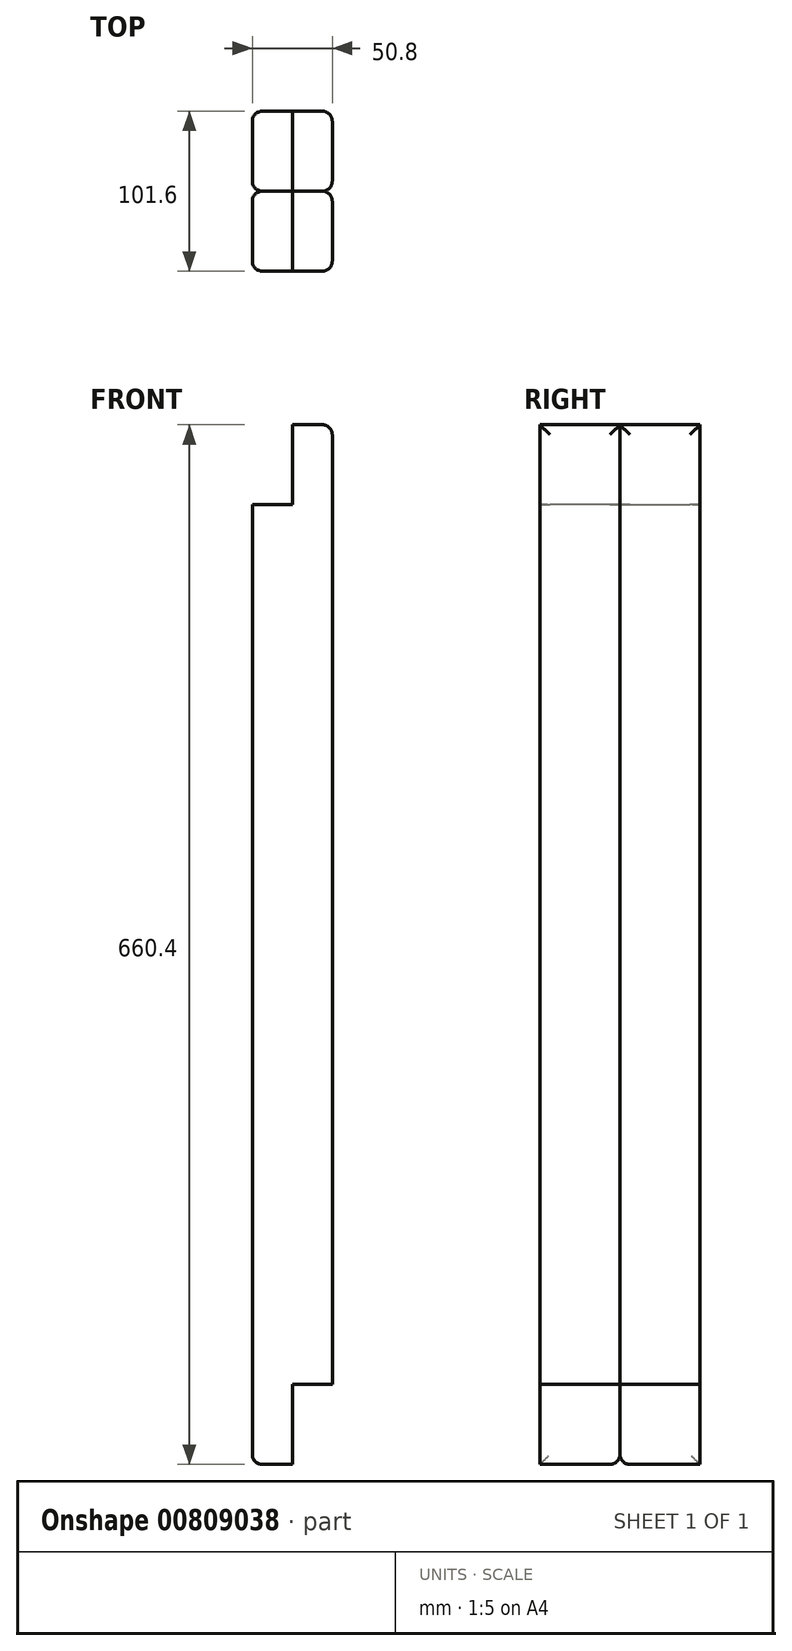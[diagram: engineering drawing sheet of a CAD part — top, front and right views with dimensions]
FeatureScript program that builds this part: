
annotation { "Feature Type Name" : "Feature", "Feature Type Description" : "" }
export const myFeature = defineFeature(function(context is Context, id is Id, definition is map)
    precondition{}
    {
        {
            var Q0;
            Q0=qCreatedBy(makeId("Top.planeOp"),FACE);
            var sketch = newSketch(context, id + "F0", { "sketchPlane" : qUnion([Q0])});
            skLineSegment(sketch, "E0.bottom", {"start": v(0, 0) * mm, "end": v(25.4, 0) * mm});
            skLineSegment(sketch, "E0.top", {"start": v(0, 50.8) * mm, "end": v(25.4, 50.8) * mm});
            skLineSegment(sketch, "E0.left", {"start": v(0, 0) * mm, "end": v(0, 50.8) * mm});
            skLineSegment(sketch, "E0.right", {"start": v(25.4, 0) * mm, "end": v(25.4, 50.8) * mm});
            skLineSegment(sketch, "E1.bottom", {"start": v(0, 0) * mm, "end": v(-25.4, 0) * mm});
            skLineSegment(sketch, "E1.top", {"start": v(0, 50.8) * mm, "end": v(-25.4, 50.8) * mm});
            skLineSegment(sketch, "E1.right", {"start": v(-25.4, 0) * mm, "end": v(-25.4, 50.8) * mm});
            skSolve(sketch);
        }
        {
            var Q0;
            Q0=makeQuery(id+"F0.imprint","IMPRINT",FACE,{"disambiguationData":[TD([[makeQuery(id+"F0.imprint","IMPRINT",EDGE,{"derivedFrom":sQuery(id+"F0.wireOp",EDGE,"E0.bottom")}),1.0]])]});
            extrude(context, id + "F1", {"entities" : qUnion([Q0]), "depth" : 609.6 * mm, "offsetDistance" : 25.4 * mm});
        }
        {
            var Q0;
            Q0=makeQuery(id+"F0.imprint","IMPRINT",FACE,{"disambiguationData":[TD([[makeQuery(id+"F0.imprint","IMPRINT",EDGE,{"derivedFrom":sQuery(id+"F0.wireOp",EDGE,"E1.bottom")}),-1.0]])]});
            extrude(context, id + "F2", {"entities" : qUnion([Q0]), "operationType" : NewBodyOperationType.ADD, "oppositeDirection" : true, "depth" : 50.8 * mm, "offsetDistance" : 25.4 * mm, "hasSecondDirection" : true, "secondDirectionOppositeDirection" : false, "secondDirectionDepth" : 558.8 * mm});
        }
        {
            var Q0;
            Q0=makeQuery(id+"F1.opExtrude","SWEPT_EDGE",EDGE,{"disambiguationData":[OSD([sQuery(id+"F0.wireOp",EDGE,"E0.bottom"),sQuery(id+"F0.wireOp",EDGE,"E0.right")])]});
            var Q1;
            Q1=makeQuery(id+"F1.opExtrude","SWEPT_EDGE",EDGE,{"disambiguationData":[OSD([sQuery(id+"F0.wireOp",EDGE,"E0.top"),sQuery(id+"F0.wireOp",EDGE,"E0.right")])]});
            var Q2;
            Q2=makeQuery(id+"F2.opExtrude","CAP_EDGE",EDGE,{"disambiguationData":[OSD([sQuery(id+"F0.wireOp",EDGE,"E1.right")])],"isStart":false});
            var Q3;
            Q3=makeQuery(id+"F2.opExtrude","SWEPT_EDGE",EDGE,{"disambiguationData":[OSD([sQuery(id+"F0.wireOp",EDGE,"E1.bottom"),sQuery(id+"F0.wireOp",EDGE,"E1.right")])]});
            var Q4;
            Q4=makeQuery(id+"F2.opExtrude","SWEPT_EDGE",EDGE,{"disambiguationData":[OSD([sQuery(id+"F0.wireOp",EDGE,"E1.top"),sQuery(id+"F0.wireOp",EDGE,"E1.right")])]});
            var Q5;
            Q5=makeQuery(id+"F2.opExtrude","CAP_EDGE",EDGE,{"disambiguationData":[OSD([sQuery(id+"F0.wireOp",EDGE,"E1.bottom")])],"isStart":false});
            var Q6;
            Q6=makeQuery(id+"F1.opExtrude","CAP_EDGE",EDGE,{"disambiguationData":[OSD([sQuery(id+"F0.wireOp",EDGE,"E0.right")])],"isStart":false});
            fillet(context, id + "F3", {"entities" : qUnion([Q0, Q1, Q2, Q3, Q4, Q5, Q6]), "radius" : 6.35 * mm, "tangentPropagation" : true, "allowEdgeOverflow" : false});
        }
        {
            var Q0;
            Q0=makeQuery(id+"F1.opExtrude","SWEPT_BODY",BODY,{"disambiguationData":[OSD([sQuery(id+"F0.wireOp",EDGE,"E0.bottom"),sQuery(id+"F0.wireOp",EDGE,"E0.top"),sQuery(id+"F0.wireOp",EDGE,"E0.right"),sQuery(id+"F0.wireOp",EDGE,"E0.left")])]});
            var Q1;
            Q1=qCreatedBy(makeId("Front.planeOp"),FACE);
            mirror(context, id + "F4", {"entities" : qUnion([Q0]), "mirrorPlane" : qUnion([Q1])});
        }
    });
